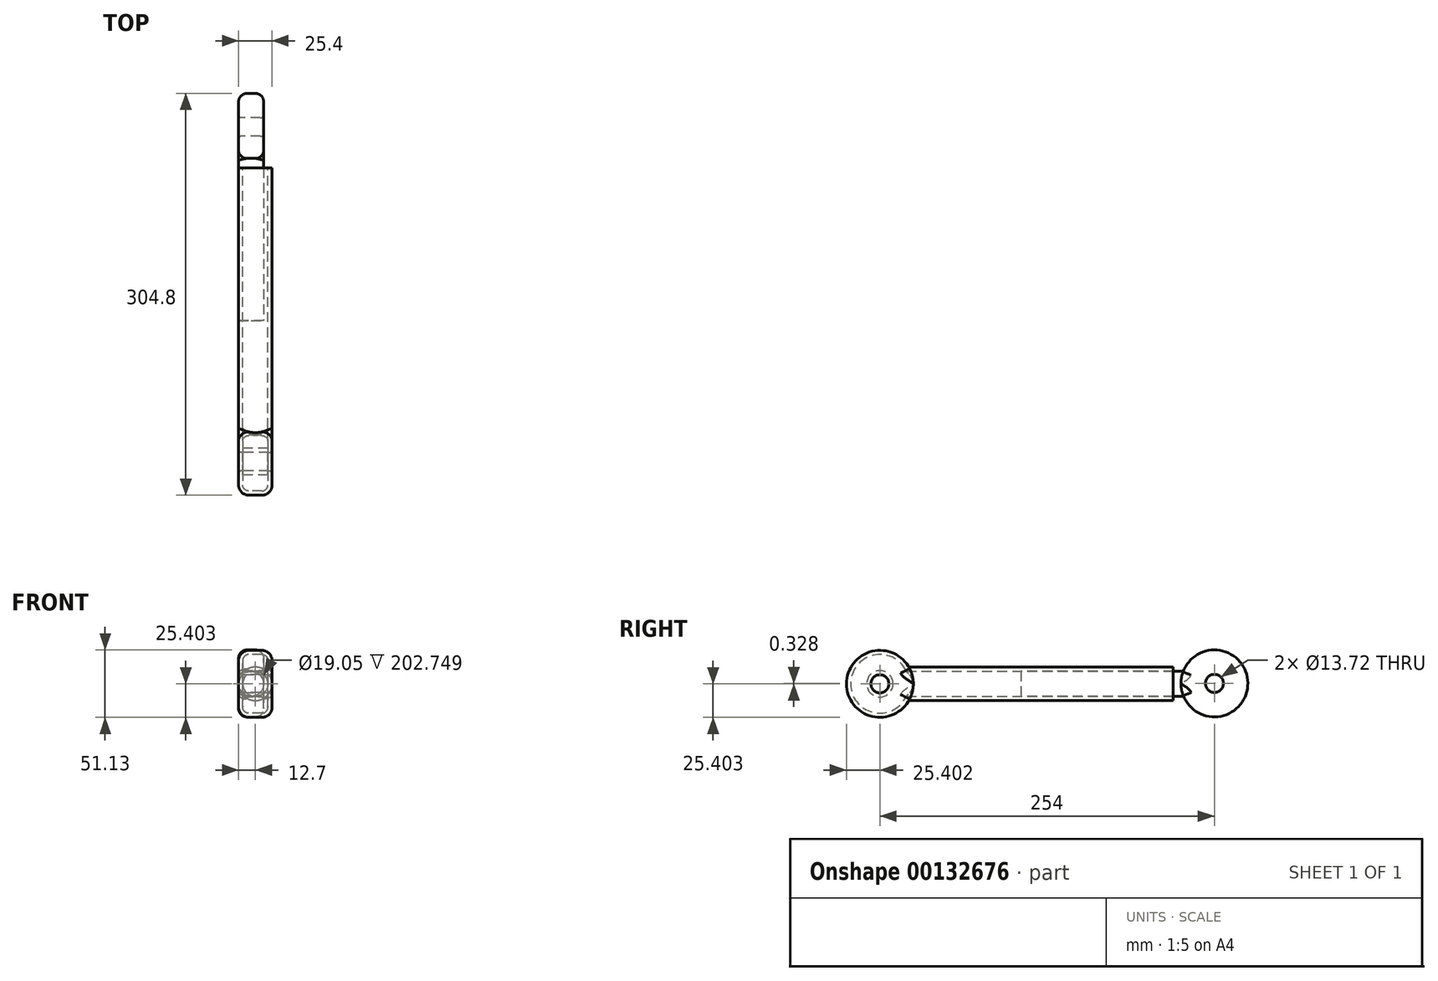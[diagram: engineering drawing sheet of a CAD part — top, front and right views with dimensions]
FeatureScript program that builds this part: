
annotation { "Feature Type Name" : "Feature", "Feature Type Description" : "" }
export const myFeature = defineFeature(function(context is Context, id is Id, definition is map)
    precondition{}
    {
        {
            var Q0;
            Q0=qCreatedBy(makeId("Right.planeOp"),FACE);
            var sketch = newSketch(context, id + "F0", { "sketchPlane" : qUnion([Q0])});
            skLineSegment(sketch, "E0.right", {"start": v(131.68, 1.02) * mm, "end": v(131.68, -24.38) * mm});
            skCircle(sketch, "E1", {"center": v(-122.32, -12) * mm, "radius": 25.4 * mm});
            skCircle(sketch, "E2", {"center": v(-122.32, -12) * mm, "radius": 6.86 * mm});
            skCircle(sketch, "E3", {"center": v(131.68, -11.68) * mm, "radius": 25.4 * mm});
            skCircle(sketch, "E4", {"center": v(131.68, -11.68) * mm, "radius": 6.86 * mm});
            skLineSegment(sketch, "E5.bottom", {"start": v(-100.32, 0.7) * mm, "end": v(100.51, 0.7) * mm});
            skLineSegment(sketch, "E5.top", {"start": v(-100.32, -24.7) * mm, "end": v(100.51, -24.7) * mm});
            skLineSegment(sketch, "E5.right", {"start": v(100.51, 0.7) * mm, "end": v(100.51, -24.7) * mm});
            skLineSegment(sketch, "E6.bottom", {"start": v(108, -2.48) * mm, "end": v(-15.22, -2.48) * mm});
            skLineSegment(sketch, "E6.top", {"start": v(108.27, -21.53) * mm, "end": v(-15.22, -21.53) * mm});
            skLineSegment(sketch, "E6.right", {"start": v(-15.22, -2.48) * mm, "end": v(-15.22, -21.53) * mm});
            skSolve(sketch);
        }
        {
            var Q0;
            {var subQ1=sQuery(id+"F0.wireOp",EDGE,"E5.bottom");Q0=makeQuery(id+"F0.imprint","IMPRINT",FACE,{"disambiguationData":[TD([[makeQuery(id+"F0.imprint","IMPRINT",EDGE,{"derivedFrom":subQ1}),-1.0]])]});}
            var Q1;
            Q1=makeQuery(id+"F0.imprint","IMPRINT",FACE,{"disambiguationData":[TD([[makeQuery(id+"F0.imprint","IMPRINT",EDGE,{"derivedFrom":sQuery(id+"F0.wireOp",EDGE,"E2")}),-1.0]])]});
            var Q2;
            {var subQ5=sQuery(id+"F0.wireOp",EDGE,"E6.right");Q2=makeQuery(id+"F0.imprint","IMPRINT",FACE,{"disambiguationData":[TD([[makeQuery(id+"F0.imprint","IMPRINT",EDGE,{"derivedFrom":subQ5}),1.0]])]});}
            extrude(context, id + "F1", {"entities" : qUnion([Q0, Q1, Q2]), "depth" : 25.4 * mm});
        }
        {
            var Q0;
            Q0=makeQuery(id+"F1.opExtrude","CAP_EDGE",EDGE,{"disambiguationData":[OSD([sQuery(id+"F0.wireOp",EDGE,"E5.bottom")])],"isStart":false});
            var Q1;
            Q1=makeQuery(id+"F1.opExtrude","CAP_EDGE",EDGE,{"disambiguationData":[OSD([sQuery(id+"F0.wireOp",EDGE,"E5.top")])],"isStart":false});
            var Q2;
            Q2=makeQuery(id+"F1.opExtrude","CAP_EDGE",EDGE,{"disambiguationData":[OSD([sQuery(id+"F0.wireOp",EDGE,"E5.bottom")])],"isStart":true});
            var Q3;
            Q3=makeQuery(id+"F1.opExtrude","CAP_EDGE",EDGE,{"disambiguationData":[OSD([sQuery(id+"F0.wireOp",EDGE,"E5.top")])],"isStart":true});
            fillet(context, id + "F2", {"entities" : qUnion([Q0, Q1, Q2, Q3]), "radius" : 12.7 * mm, "tangentPropagation" : true, "allowEdgeOverflow" : false});
        }
        {
            var Q0;
            Q0=makeQuery(id+"F1.opExtrude","CAP_EDGE",EDGE,{"disambiguationData":[OSD([sQuery(id+"F0.wireOp",EDGE,"E1")])],"isStart":false});
            var Q1;
            Q1=makeQuery(id+"F1.opExtrude","CAP_EDGE",EDGE,{"disambiguationData":[OSD([sQuery(id+"F0.wireOp",EDGE,"E1")])],"isStart":true});
            fillet(context, id + "F3", {"entities" : qUnion([Q0, Q1]), "radius" : 7.62 * mm, "tangentPropagation" : true, "allowEdgeOverflow" : false});
        }
        {
            var Q0;
            Q0=makeQuery(id+"F1.opExtrude","CAP_EDGE",EDGE,{"disambiguationData":[OSD([sQuery(id+"F0.wireOp",EDGE,"E2")])],"isStart":false});
            var Q1;
            Q1=makeQuery(id+"F1.opExtrude","CAP_EDGE",EDGE,{"disambiguationData":[OSD([sQuery(id+"F0.wireOp",EDGE,"E2")])],"isStart":true});
            fillet(context, id + "F4", {"entities" : qUnion([Q0, Q1]), "radius" : 2.54 * mm, "tangentPropagation" : true, "allowEdgeOverflow" : false});
        }
        {
            var Q0;
            Q0=makeQuery(id+"F1.opExtrude","SWEPT_FACE",FACE,{"disambiguationData":[OSD([sQuery(id+"F0.wireOp",EDGE,"E5.right")])]});
            shell(context, id + "F5", {"entities" : qUnion([Q0]), "thickness" : 3.17 * mm});
        }
        {
            var Q0;
            {var subQ0=sQuery(id+"F0.wireOp",EDGE,"E3");var subQ1=makeQuery(id+"F0.imprint","INTERSECT",VERTEX,{"derivedFrom":[subQ0,sQuery(id+"F0.wireOp",EDGE,"E6.bottom")]});Q0=makeQuery(id+"F0.imprint","IMPRINT",FACE,{"disambiguationData":[TD([[makeQuery(id+"F0.imprint","IMPRINT",EDGE,{"disambiguationData":[TD([[subQ1,-1.0]])],"derivedFrom":subQ0}),1.0]])]});}
            var Q1;
            {var subQ0=sQuery(id+"F0.wireOp",EDGE,"E6.bottom");var subQ1=sQuery(id+"F0.wireOp",EDGE,"E3");var subQ2=makeQuery(id+"F0.imprint","INTERSECT",VERTEX,{"derivedFrom":[subQ1,subQ0]});Q1=makeQuery(id+"F0.imprint","IMPRINT",FACE,{"disambiguationData":[TD([[makeQuery(id+"F0.imprint","IMPRINT",EDGE,{"disambiguationData":[TD([[subQ2,-1.0]])],"derivedFrom":subQ1}),-1.0]])]});}
            var Q2;
            {var subQ5=sQuery(id+"F0.wireOp",EDGE,"E6.right");Q2=makeQuery(id+"F0.imprint","IMPRINT",FACE,{"disambiguationData":[TD([[makeQuery(id+"F0.imprint","IMPRINT",EDGE,{"derivedFrom":subQ5}),1.0]])]});}
            extrude(context, id + "F6", {"entities" : qUnion([Q0, Q1, Q2]), "depth" : 19.05 * mm});
        }
        {
            var Q0;
            Q0=makeQuery(id+"F6.opExtrude","CAP_EDGE",EDGE,{"disambiguationData":[OSD([sQuery(id+"F0.wireOp",EDGE,"E6.bottom")])],"isStart":true});
            var Q1;
            Q1=makeQuery(id+"F6.opExtrude","CAP_EDGE",EDGE,{"disambiguationData":[OSD([sQuery(id+"F0.wireOp",EDGE,"E6.top")])],"isStart":true});
            var Q2;
            Q2=makeQuery(id+"F6.opExtrude","CAP_EDGE",EDGE,{"disambiguationData":[OSD([sQuery(id+"F0.wireOp",EDGE,"E6.bottom")])],"isStart":false});
            var Q3;
            Q3=makeQuery(id+"F6.opExtrude","CAP_EDGE",EDGE,{"disambiguationData":[OSD([sQuery(id+"F0.wireOp",EDGE,"E6.top")])],"isStart":false});
            fillet(context, id + "F7", {"entities" : qUnion([Q0, Q1, Q2, Q3]), "radius" : 9.52 * mm, "tangentPropagation" : true, "allowEdgeOverflow" : false});
        }
        {
            var Q0;
            Q0=makeQuery(id+"F6.opExtrude","CAP_EDGE",EDGE,{"disambiguationData":[OSD([sQuery(id+"F0.wireOp",EDGE,"E3")])],"isStart":true});
            var Q1;
            Q1=makeQuery(id+"F6.opExtrude","CAP_EDGE",EDGE,{"disambiguationData":[OSD([sQuery(id+"F0.wireOp",EDGE,"E3")])],"isStart":false});
            fillet(context, id + "F8", {"entities" : qUnion([Q0, Q1]), "radius" : 6.35 * mm, "tangentPropagation" : true, "allowEdgeOverflow" : false});
        }
        {
            var Q0;
            Q0=makeQuery(id+"F6.opExtrude","CAP_EDGE",EDGE,{"disambiguationData":[OSD([sQuery(id+"F0.wireOp",EDGE,"E4")])],"isStart":false});
            var Q1;
            Q1=makeQuery(id+"F6.opExtrude","CAP_EDGE",EDGE,{"disambiguationData":[OSD([sQuery(id+"F0.wireOp",EDGE,"E4")])],"isStart":true});
            fillet(context, id + "F9", {"entities" : qUnion([Q0, Q1]), "radius" : 2.54 * mm, "tangentPropagation" : true, "allowEdgeOverflow" : false});
        }
    });
